# Revit family: Nuaire_IfcFanType_MevEco
name_source: partatom
category: Mechanical Equipment
revit_build: Autodesk Revit 2018 (Build: 20170223_1515(x64)
units: mm (PartAtom-declared; Revit-internal decimal feet)

## family parameters
Always vertical = Yes
Cut with Voids When Loaded = No
OmniClass Number = 23.75.00.00
OmniClass Title = Climate Control (HVAC)
Part Type = Normal
Room Calculation Point = No
Round Connector Dimension = Use Radius
Shared = No
Work Plane-Based = No

## types (2) — shared parameters
6 Monthly = SFG20 20-03
Annually = SFG20 20-03
Apparent Load = 151.80 VA
BMS Links = No
Battery Supply = No
CE Approval = Yes
COBie.Type = Yes
COBie.Type.Category = Pr_65_67_29_12 : Centrifugal fans
COBie.Type.Length = 596 mm  [stored 1.95538 ft]
COBie.Type.Manufacturer = Nuaire
COBie.Type.NominalHeight = 125 mm  [stored 0.410105 ft]
COBie.Type.NominalLength = 596 mm  [stored 1.95538 ft]
COBie.Type.NominalWidth = 340 mm  [stored 1.11549 ft]
COBie.Type.WarrantyDescription = 5 years. First year parts and labour, remaining 4 years parts only.
COBie.Type.WarrantyDurationLabor = 1
COBie.Type.WarrantyDurationParts = 5
COBie.Type.WarrantyDurationUnit = Year
COBie.Type.WarrantyGuarantorLabor = Nuaire
COBie.Type.WarrantyGuarantorParts = Nuaire
Catalogue Pages = http://nuaire.info
Classification.Uniclass.Pr.Description = Centrifugal fans
Classification.Uniclass.Pr.Number = Pr_65_67_29_12
Daily = SFG20 20-03
Duct Connection Height = 60 mm  [stored 0.19685 ft]
Duct Connection Width = 204 mm
Enclosure Rating = Not IP rated
Environmental Product Declaration = WEEE, RoHS
Fax Number = +44(0)2920-858-222
Fire Control Panel Links = No
Frequency = 50.00 Hz
Full Load Current = 0.66 A
Height = 125 mm  [stored 0.410105 ft]
I&M Manual = http://nuaire.info
IFCExportAs = IfcFanType
IFCExportType = CENTRIFUGALBACKWARDINCLINEDCURVED
Length = 596 mm  [stored 1.95538 ft]
Location of Manufacturer = 51.571856, -3.232638
Maintenance Required 0 to 300hrs = http://nuaire.info
Maintenance Required 1001 to 2000hrs = http://nuaire.info
Maintenance Required 2001 to 4000hrs = http://nuaire.info
Maintenance Required 301 to 600hrs = http://nuaire.info
Maintenance Required 4001 to 8000hrs = http://nuaire.info
Maintenance Required 601 to 1000hrs = http://nuaire.info
Maintenance Required 8001 to 12000hrs = http://nuaire.info
Manufacturer = Nuaire
Manufacturer Website = http://www.nuaire.co.uk
Maximum Ambient Temperature = 50.00 °C
Monthly = SFG20 20-03
Nominal Motor Rating = 0.087 kW
Nominal Motor Speed (rpm) = 3300
Number of Connection Poles = 2
OmniClass Number = 23-33 31 19 13
OmniClass Title = Centrifugal fans
Operation and Maintenance Manual = http://nuaire.info
Postcode = CF83 1NA
Power Source = Mains
Product Literature = http://nuaire.info
Product Range = MEV-ECO
Quarterly = SFG20 20-03
Reference Standard = ISO 9001:2015
Responsible Sourcing of Materials = FSC
Revit Family Last Revised = 2020-09-23T13:00:00
Starting Current = 0.45 A
Supply Phase = 1
Telephone Number = +44(0)2920-858-200
URL = http://www.nuaire.co.uk
Voltage = 230.00 V
Weatherproof or Internal Only = Internal only
Weekly = SFG20 20-03
Weight = 4.00 kg
Width = 340 mm  [stored 1.11549 ft]
zero-valued in all types: COBie.Type.Area, COBie.Type.ReplacementCost, Life Cycle Analysis

## per-type parameters (varying)
| type | 3button | 4button | COBie.Type.Description | Description |
| MEV-ECO | Yes | No | Mechanical extract ventilation system with multi-spigot option | Mechanical extract ventilation system with multi-spigot option |
| MEV-ECO-H | No | Yes | Mechanical extract ventilation system with multi-spigot option and humidistat | Mechanical extract ventilation system with multi-spigot option and humidistat |

note: column(s) folded — value = type name in every type: COBie.Type.ModelNumber, COBie.Type.ModelReference, COBie.Type.Name, Model

note: [stored X ft] marks values corroborated as IEEE doubles in the binary element streams (Revit-internal decimal feet)

## geometry (parser evidence)
native form markers: Blend x8, Sweep x2
no freeform markers — native parametric forms only
